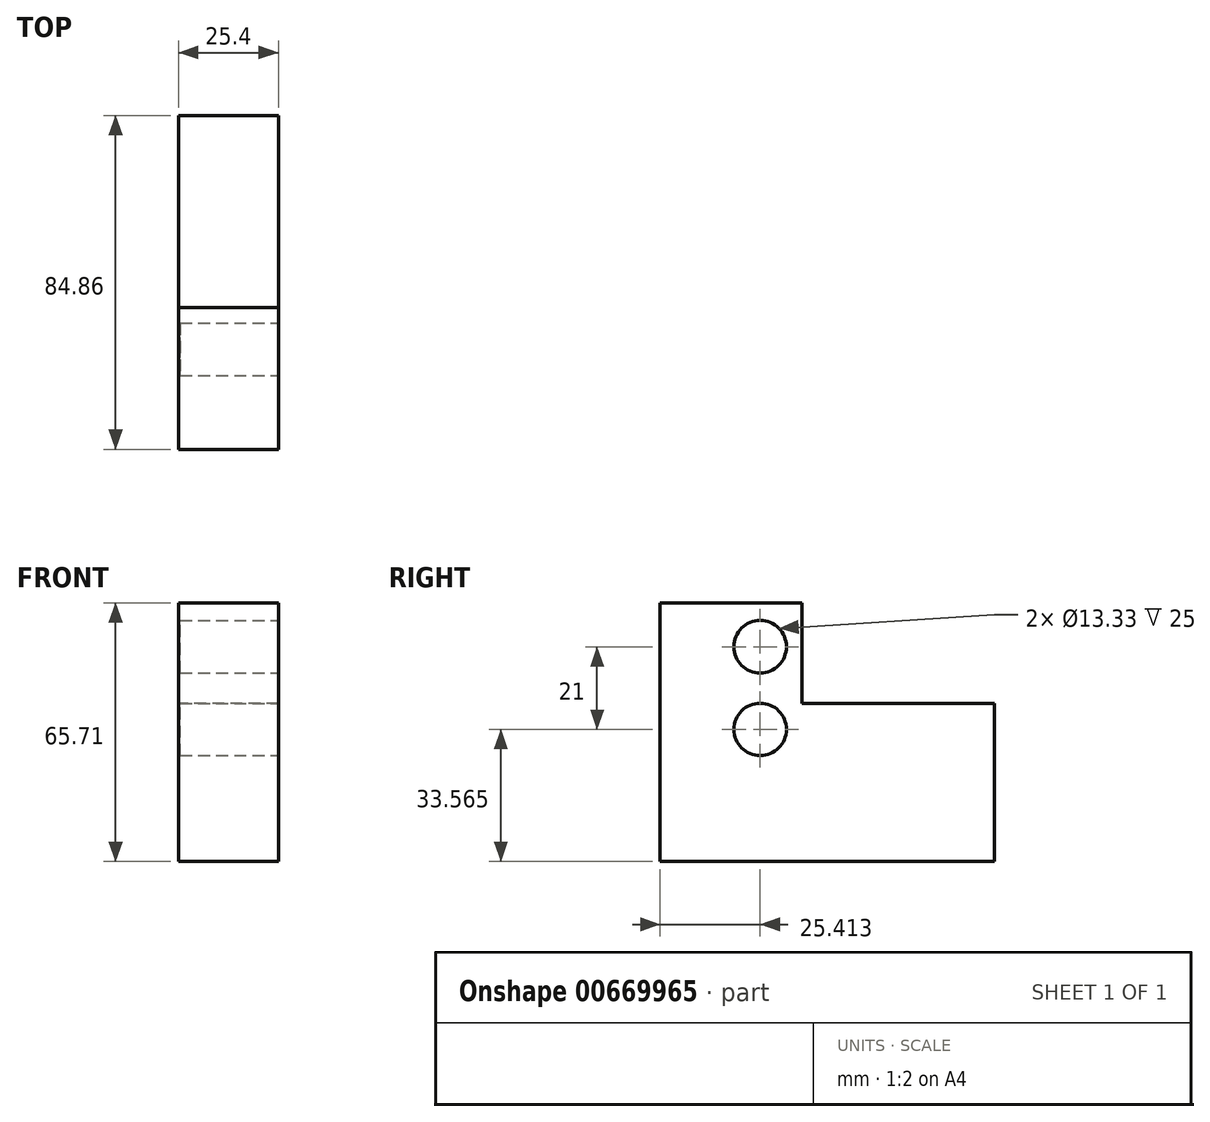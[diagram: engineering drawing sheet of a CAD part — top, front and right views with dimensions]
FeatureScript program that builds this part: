
annotation { "Feature Type Name" : "Feature", "Feature Type Description" : "" }
export const myFeature = defineFeature(function(context is Context, id is Id, definition is map)
    precondition{}
    {
        {
            var Q0;
            Q0=qCreatedBy(makeId("Right.planeOp"),FACE);
            var sketch = newSketch(context, id + "F0", { "sketchPlane" : qUnion([Q0])});
            skLineSegment(sketch, "E0.bottom", {"start": v(0, 0) * mm, "end": v(84.86, 0) * mm});
            skLineSegment(sketch, "E0.top", {"start": v(0, 40.23) * mm, "end": v(84.86, 40.23) * mm});
            skLineSegment(sketch, "E0.left", {"start": v(0, 0) * mm, "end": v(0, 40.23) * mm});
            skLineSegment(sketch, "E0.right", {"start": v(84.86, 0) * mm, "end": v(84.86, 40.23) * mm});
            skLineSegment(sketch, "E1.bottom", {"start": v(0, 40.23) * mm, "end": v(36.02, 40.23) * mm});
            skLineSegment(sketch, "E1.top", {"start": v(0, 65.7) * mm, "end": v(36.02, 65.7) * mm});
            skLineSegment(sketch, "E1.left", {"start": v(0, 40.23) * mm, "end": v(0, 65.7) * mm});
            skLineSegment(sketch, "E1.right", {"start": v(36.02, 40.23) * mm, "end": v(36.02, 65.7) * mm});
            skSolve(sketch);
        }
        {
            var Q0;
            Q0=qSketchRegion(id+"F0",true);
            extrude(context, id + "F1", {"entities" : qUnion([Q0]), "depth" : 25.4 * mm, "offsetDistance" : 25.4 * mm});
        }
        {
            var Q0;
            Q0=makeQuery(id+"F1.opExtrude","CAP_FACE",FACE,{"disambiguationData":[OSD([sQuery(id+"F0.wireOp",EDGE,"E0.bottom"),sQuery(id+"F0.wireOp",EDGE,"E0.top"),sQuery(id+"F0.wireOp",EDGE,"E0.left"),sQuery(id+"F0.wireOp",EDGE,"E0.right"),sQuery(id+"F0.wireOp",EDGE,"E1.top"),sQuery(id+"F0.wireOp",EDGE,"E1.left"),sQuery(id+"F0.wireOp",EDGE,"E1.right")])],"isStart":false});
            var sketch = newSketch(context, id + "F2", { "sketchPlane" : qUnion([Q0])});
            skCircle(sketch, "E2", {"center": v(25.41, 33.56) * mm, "radius": 6.66 * mm});
            skCircle(sketch, "E3.0.1.0", {"center": v(25.41, 54.56) * mm, "radius": 6.66 * mm});
            skLineSegment(sketch, "E3.direction1", {"start": v(25.41, 33.56) * mm, "end": v(50.41, 33.56) * mm, "construction": true});
            skLineSegment(sketch, "E3.direction2", {"start": v(25.41, 33.56) * mm, "end": v(25.41, 54.56) * mm, "construction": true});
            skSolve(sketch);
        }
        {
            var Q0;
            Q0 = qSketchRegion(id + "F2", true);
            extrude(context, id + "F3", {"entities" : qUnion([Q0]), "operationType" : NewBodyOperationType.REMOVE, "oppositeDirection" : true, "depth" : 25 * mm, "offsetDistance" : 25 * mm});
        }
    });
